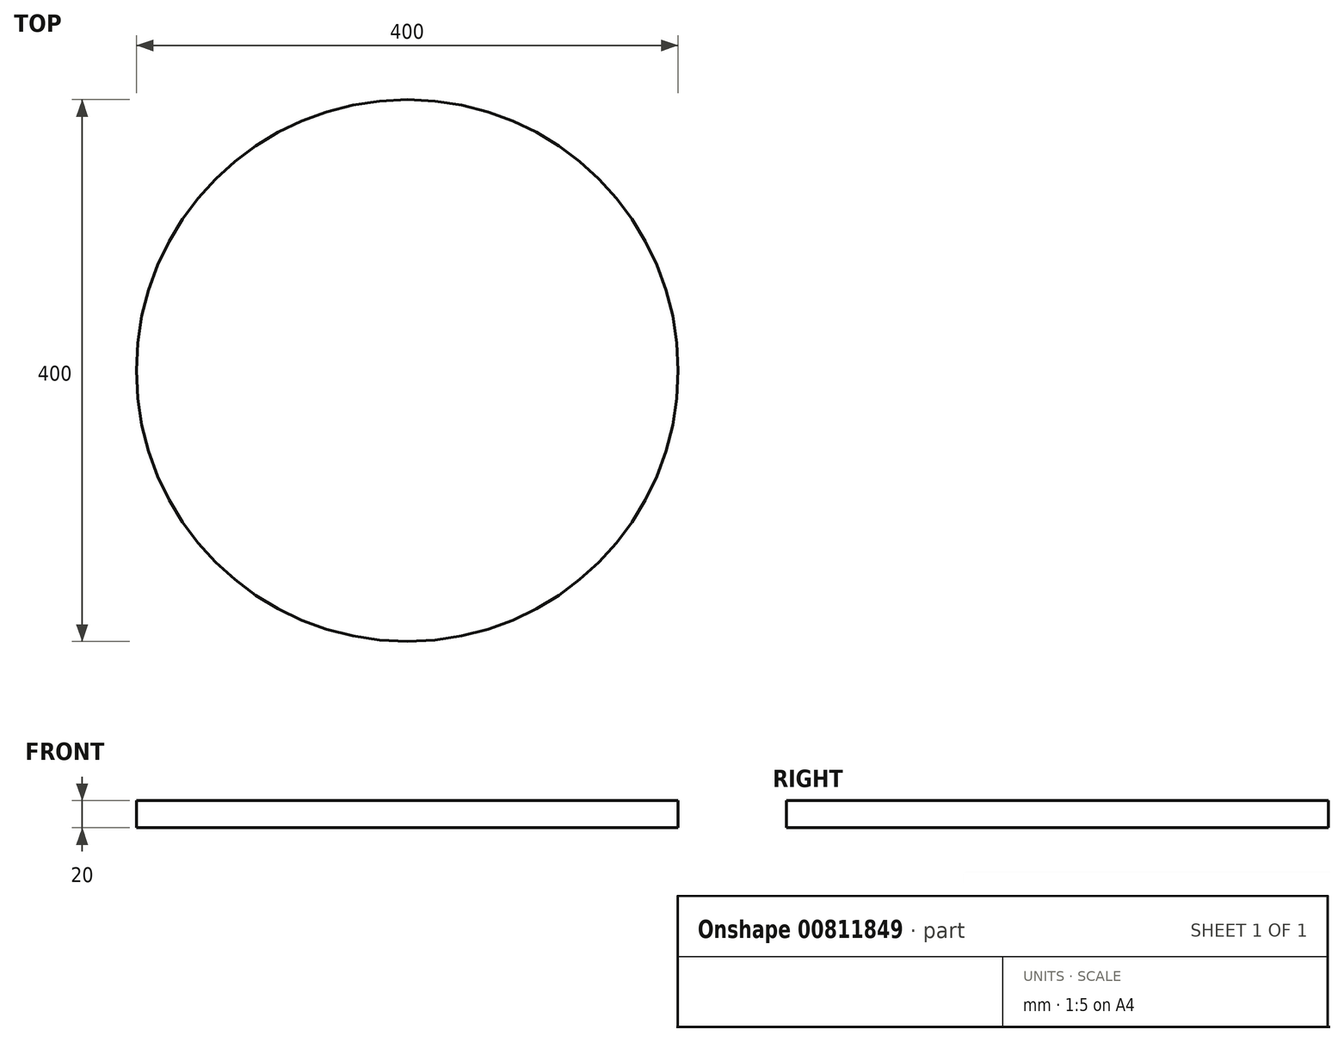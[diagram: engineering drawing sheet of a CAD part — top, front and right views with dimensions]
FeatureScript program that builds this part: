
annotation { "Feature Type Name" : "Feature", "Feature Type Description" : "" }
export const myFeature = defineFeature(function(context is Context, id is Id, definition is map)
    precondition{}
    {
        {
            var Q0;
            Q0=qCreatedBy(makeId("Top.planeOp"),FACE);
            var sketch = newSketch(context, id + "F0", { "sketchPlane" : qUnion([Q0])});
            skCircle(sketch, "E0", {"center": v(0, 0) * mm, "radius": 200 * mm});
            skSolve(sketch);
        }
        {
            var Q0;
            Q0 = qSketchRegion(id + "F0", true);
            extrude(context, id + "F1", {"entities" : qUnion([Q0]), "depth" : 20 * mm, "offsetDistance" : 25 * mm});
        }
    });
